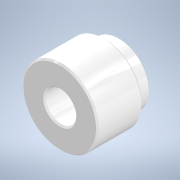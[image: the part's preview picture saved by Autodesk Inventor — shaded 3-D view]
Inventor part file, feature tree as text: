
AUTODESK INVENTOR PART (.ipt)
format: ipt  version: 2021 (Build 250183000, 183)  size: 133,632 bytes
history: native  units: mm
features: other x3, extrude x2, sketch x2, chamfer x1, reference x1
ambient origin geometry x8: Origin, YZ Plane, XZ Plane, XY Plane, X Axis, Y Axis, Z Axis, Center Point
bodies: Body1 (feature_tree)
feature tree (9):
  other  "Bryła1"
  extrude  "Wyciągnięcie proste1"  Depth=20.0mm
  extrude  "Wyciągnięcie proste2"  Depth=10.0mm TaperAngle=0.0deg
  chamfer  "Faza1"  Distance=50.0mm
  sketch  "Szkic1"
  reference  "Odniesienie1"
  sketch  "Szkic2"
  other  "wszystko.iam"
  other  "dekieltop:1"
